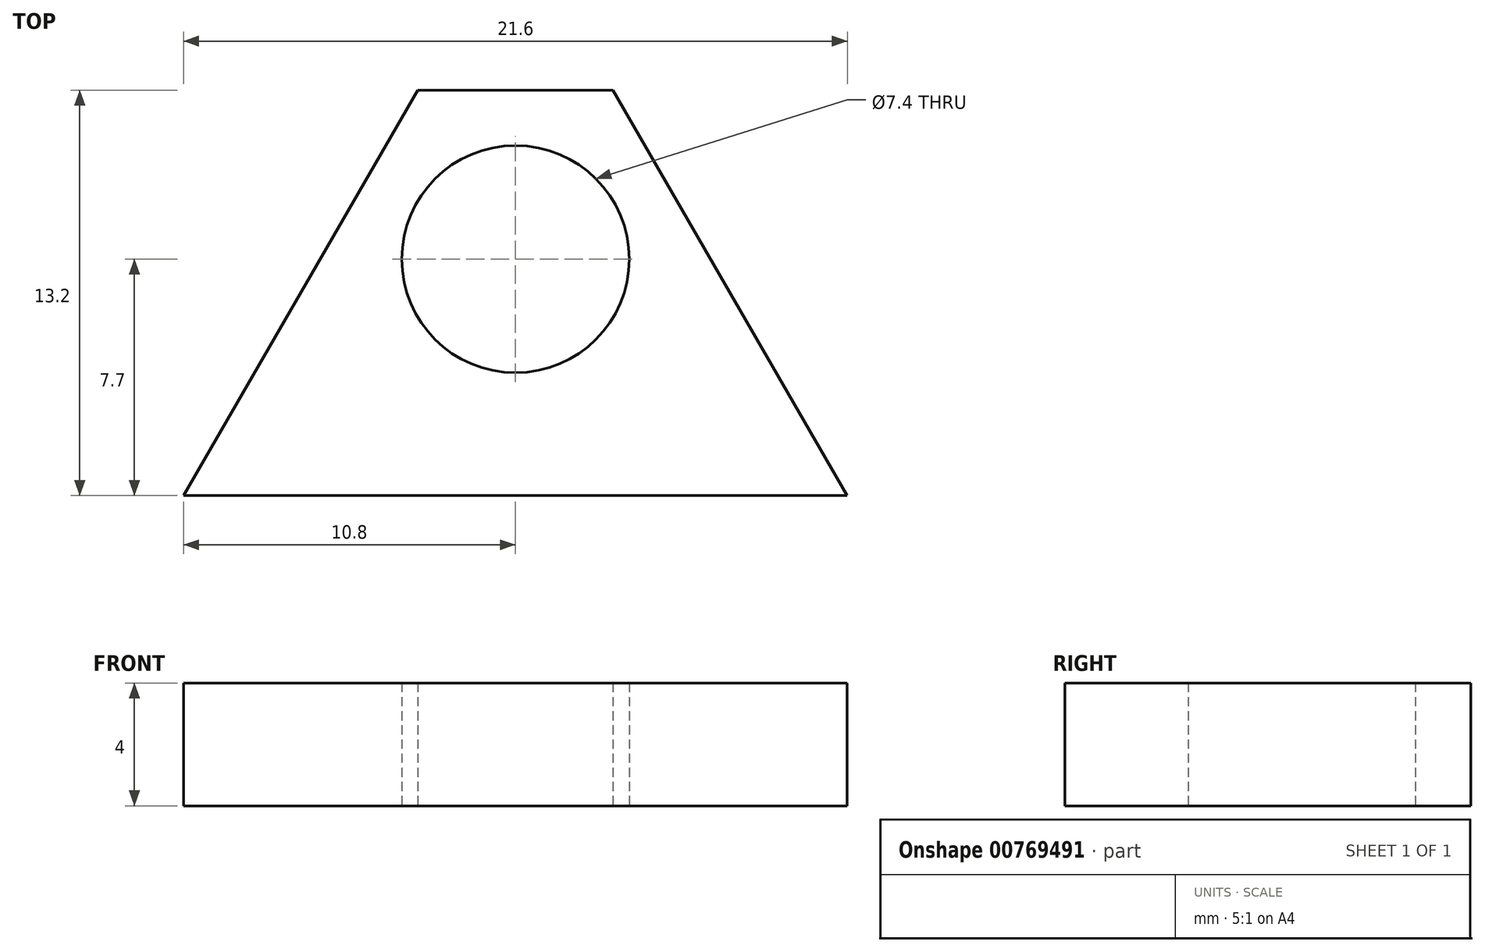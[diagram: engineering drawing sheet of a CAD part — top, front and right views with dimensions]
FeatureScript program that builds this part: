
annotation { "Feature Type Name" : "Feature", "Feature Type Description" : "" }
export const myFeature = defineFeature(function(context is Context, id is Id, definition is map)
    precondition{}
    {
        {
            var Q0;
            Q0=qCreatedBy(makeId("Top.planeOp"),FACE);
            var sketch = newSketch(context, id + "F0", { "sketchPlane" : qUnion([Q0])});
            skCircle(sketch, "E0.cCircle", {"center": v(0, 7.7) * mm, "radius": 5.5 * mm, "construction": true});
            skLineSegment(sketch, "E0.2", {"start": v(-6.35, 7.7) * mm, "end": v(-3.18, 13.2) * mm});
            skLineSegment(sketch, "E0.3", {"start": v(-3.18, 13.2) * mm, "end": v(3.18, 13.2) * mm});
            skLineSegment(sketch, "E0.4", {"start": v(3.18, 13.2) * mm, "end": v(6.93, 6.7) * mm});
            skPoint(sketch, "E0.0.midPoint", {"position": v(0, 2.2) * mm});
            skLineSegment(sketch, "E1", {"start": v(-6.35, 7.7) * mm, "end": v(-10.8, 0) * mm});
            skLineSegment(sketch, "E2", {"start": v(-10.8, 0) * mm, "end": v(10.8, 0) * mm});
            skLineSegment(sketch, "E3", {"start": v(10.8, 0) * mm, "end": v(6.93, 6.7) * mm});
            skCircle(sketch, "E4", {"center": v(0, 7.7) * mm, "radius": 3.7 * mm});
            skSolve(sketch);
        }
        {
            var Q0;
            Q0=makeQuery(id+"F0.imprint","IMPRINT",FACE,{"disambiguationData":[TD([[makeQuery(id+"F0.imprint","IMPRINT",EDGE,{"derivedFrom":sQuery(id+"F0.wireOp",EDGE,"E0.2")}),-1.0]])]});
            extrude(context, id + "F1", {"entities" : qUnion([Q0]), "depth" : 4 * mm, "offsetDistance" : 25 * mm});
        }
    });
